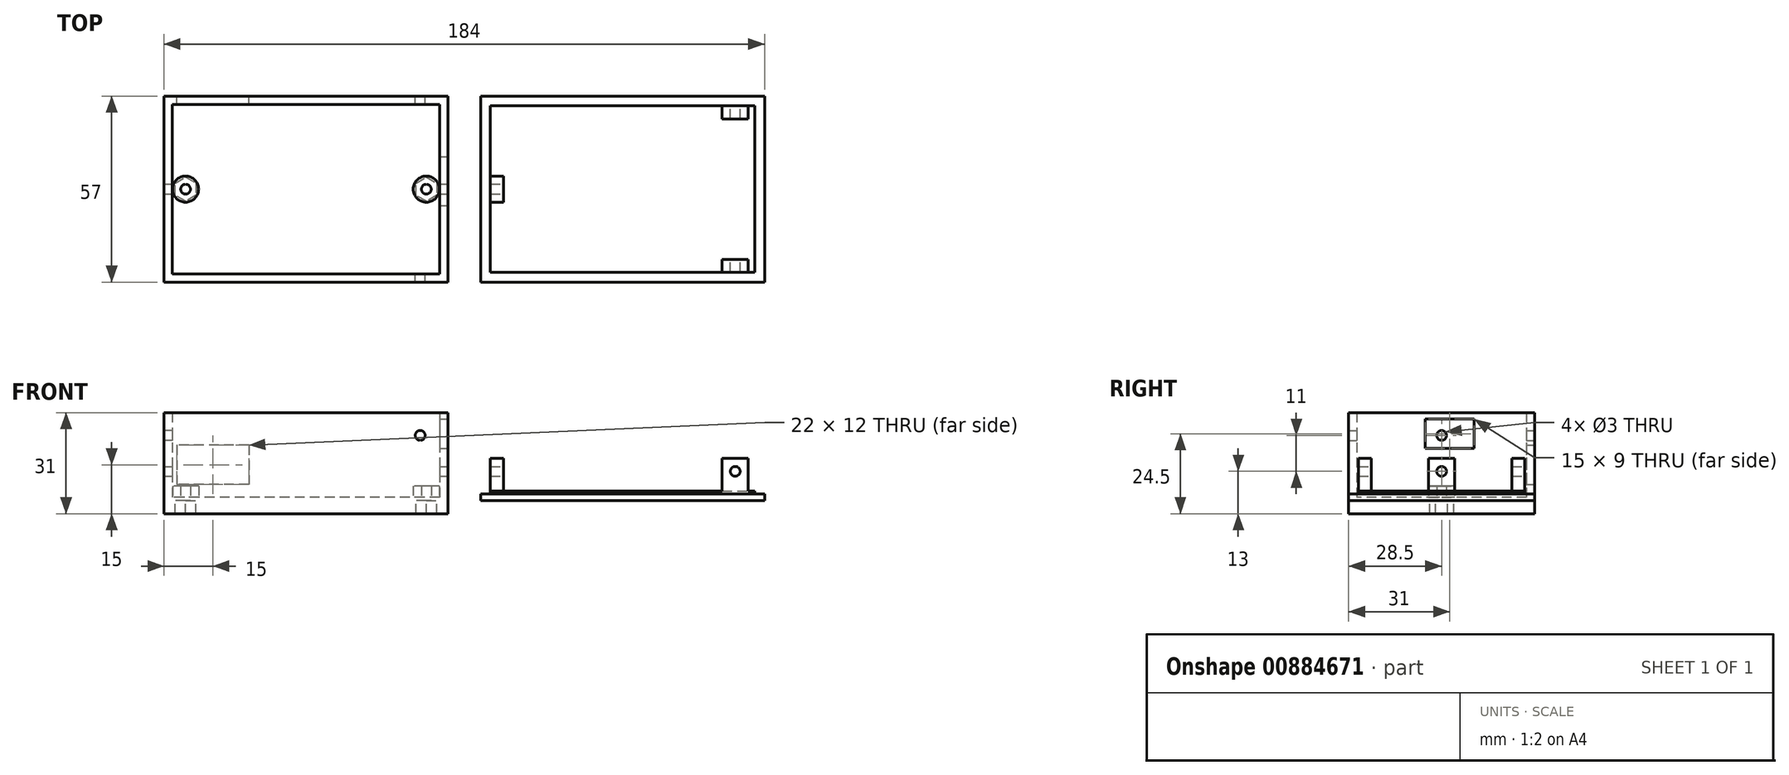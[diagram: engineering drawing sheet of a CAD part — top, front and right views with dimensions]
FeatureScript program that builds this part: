
annotation { "Feature Type Name" : "Feature", "Feature Type Description" : "" }
export const myFeature = defineFeature(function(context is Context, id is Id, definition is map)
    precondition{}
    {
        {
            assignVariable(context, id + "F0", {"name" : "wThickness", "anyValue" : 2.5});
        }
        {
            assignVariable(context, id + "F1", {"name" : "bThickness", "anyValue" : 5});
        }
        {
            assignVariable(context, id + "F2", {"name" : "nutThick", "anyValue" : 4});
        }
        {
            var Q0;
            Q0=qCreatedBy(makeId("Top.planeOp"),FACE);
            var sketch = newSketch(context, id + "F3", { "sketchPlane" : qUnion([Q0])});
            skLineSegment(sketch, "E0.bottom", {"start": v(0, 0) * mm, "end": v(87, 0) * mm});
            skLineSegment(sketch, "E0.top", {"start": v(0, 57) * mm, "end": v(87, 57) * mm});
            skLineSegment(sketch, "E0.left", {"start": v(0, 0) * mm, "end": v(0, 57) * mm});
            skLineSegment(sketch, "E0.right", {"start": v(87, 0) * mm, "end": v(87, 57) * mm});
            skLineSegment(sketch, "E1.bottom", {"start": v(2.5, 2.5) * mm, "end": v(84.5, 2.5) * mm});
            skLineSegment(sketch, "E1.top", {"start": v(2.5, 54.5) * mm, "end": v(84.5, 54.5) * mm});
            skLineSegment(sketch, "E1.left", {"start": v(2.5, 2.5) * mm, "end": v(2.5, 54.5) * mm});
            skLineSegment(sketch, "E1.right", {"start": v(84.5, 2.5) * mm, "end": v(84.5, 54.5) * mm});
            skLineSegment(sketch, "E2", {"start": v(2.5, 2.5) * mm, "end": v(2.5, 0) * mm, "construction": true});
            skLineSegment(sketch, "E3", {"start": v(2.5, 2.5) * mm, "end": v(0, 2.5) * mm, "construction": true});
            skLineSegment(sketch, "E4", {"start": v(43.5, 54.5) * mm, "end": v(43.5, 2.5) * mm, "construction": true});
            skLineSegment(sketch, "E5", {"start": v(43.5, 28.5) * mm, "end": v(6.63, 28.5) * mm, "construction": true});
            skCircle(sketch, "E6", {"center": v(6.63, 28.5) * mm, "radius": 1.5 * mm});
            skCircle(sketch, "E7.cCircle", {"center": v(6.63, 28.5) * mm, "radius": 3.2 * mm, "construction": true});
            skLineSegment(sketch, "E7.0", {"start": v(9.83, 30.35) * mm, "end": v(9.83, 26.65) * mm});
            skLineSegment(sketch, "E7.1", {"start": v(9.83, 26.65) * mm, "end": v(6.63, 24.8) * mm});
            skLineSegment(sketch, "E7.2", {"start": v(6.63, 24.8) * mm, "end": v(3.43, 26.65) * mm});
            skLineSegment(sketch, "E7.3", {"start": v(3.43, 26.65) * mm, "end": v(3.43, 30.35) * mm});
            skLineSegment(sketch, "E7.4", {"start": v(3.43, 30.35) * mm, "end": v(6.63, 32.2) * mm});
            skLineSegment(sketch, "E7.5", {"start": v(6.63, 32.2) * mm, "end": v(9.83, 30.35) * mm});
            skPoint(sketch, "E7.0.midPoint", {"position": v(9.83, 28.5) * mm});
            skCircle(sketch, "E8", {"center": v(80.38, 28.5) * mm, "radius": 1.5 * mm});
            skCircle(sketch, "E9.cCircle", {"center": v(80.38, 28.5) * mm, "radius": 3.2 * mm, "construction": true});
            skLineSegment(sketch, "E9.0", {"start": v(83.58, 30.35) * mm, "end": v(83.58, 26.65) * mm});
            skLineSegment(sketch, "E9.1", {"start": v(83.57, 26.65) * mm, "end": v(80.37, 24.8) * mm});
            skLineSegment(sketch, "E9.2", {"start": v(80.38, 24.8) * mm, "end": v(77.18, 26.65) * mm});
            skLineSegment(sketch, "E9.3", {"start": v(77.17, 26.65) * mm, "end": v(77.17, 30.35) * mm});
            skLineSegment(sketch, "E9.4", {"start": v(77.17, 30.35) * mm, "end": v(80.37, 32.2) * mm});
            skLineSegment(sketch, "E9.5", {"start": v(80.38, 32.2) * mm, "end": v(83.58, 30.35) * mm});
            skPoint(sketch, "E9.0.midPoint", {"position": v(83.58, 28.5) * mm});
            skLineSegment(sketch, "E10", {"start": v(43.5, 28.5) * mm, "end": v(80.38, 28.5) * mm, "construction": true});
            skPoint(sketch, "E11", {"position": v(77.17, 28.5) * mm});
            skLineSegment(sketch, "E12", {"start": v(87, 57) * mm, "end": v(97, 57) * mm, "construction": true});
            skLineSegment(sketch, "E13.bottom", {"start": v(97, 57) * mm, "end": v(184, 57) * mm});
            skLineSegment(sketch, "E13.top", {"start": v(97, 0) * mm, "end": v(184, 0) * mm});
            skLineSegment(sketch, "E13.left", {"start": v(97, 57) * mm, "end": v(97, 0) * mm});
            skLineSegment(sketch, "E13.right", {"start": v(184, 57) * mm, "end": v(184, 0) * mm});
            skLineSegment(sketch, "E14.bottom", {"start": v(181, 3) * mm, "end": v(100, 3) * mm});
            skLineSegment(sketch, "E14.top", {"start": v(181, 54) * mm, "end": v(100, 54) * mm});
            skLineSegment(sketch, "E14.left", {"start": v(181, 3) * mm, "end": v(181, 54) * mm});
            skLineSegment(sketch, "E14.right", {"start": v(100, 3) * mm, "end": v(100, 54) * mm});
            skLineSegment(sketch, "E15", {"start": v(100, 3) * mm, "end": v(97, 3) * mm, "construction": true});
            skLineSegment(sketch, "E16", {"start": v(100, 3) * mm, "end": v(100, 0) * mm, "construction": true});
            skSolve(sketch);
        }
        {
            var Q0;
            Q0=makeQuery(id+"F3.imprint","IMPRINT",FACE,{"disambiguationData":[TD([[makeQuery(id+"F3.imprint","IMPRINT",EDGE,{"derivedFrom":sQuery(id+"F3.wireOp",EDGE,"E0.bottom")}),1.0]])]});
            var Q1;
            Q1=makeQuery(id+"F3.imprint","IMPRINT",FACE,{"disambiguationData":[TD([[makeQuery(id+"F3.imprint","IMPRINT",EDGE,{"derivedFrom":sQuery(id+"F3.wireOp",EDGE,"E1.bottom")}),1.0]])]});
            extrude(context, id + "F4", {"entities" : qUnion([Q0, Q1]), "oppositeDirection" : true, "depth" : (getVariable(context, 'nutThick')) * mm, "offsetDistance" : 25 * mm});
        }
        {
            var Q0;
            Q0=makeQuery(id+"F3.imprint","IMPRINT",FACE,{"disambiguationData":[TD([[makeQuery(id+"F3.imprint","IMPRINT",EDGE,{"derivedFrom":sQuery(id+"F3.wireOp",EDGE,"E1.bottom")}),1.0]])]});
            var Q1;
            Q1=makeQuery(id+"F3.imprint","IMPRINT",FACE,{"disambiguationData":[TD([[makeQuery(id+"F3.imprint","IMPRINT",EDGE,{"derivedFrom":sQuery(id+"F3.wireOp",EDGE,"E0.bottom")}),1.0]])]});
            var Q2;
            Q2=makeQuery(id+"F3.imprint","IMPRINT",FACE,{"disambiguationData":[TD([[makeQuery(id+"F3.imprint","IMPRINT",EDGE,{"derivedFrom":sQuery(id+"F3.wireOp",EDGE,"E6")}),-1.0]])]});
            var Q3;
            Q3=makeQuery(id+"F3.imprint","IMPRINT",FACE,{"disambiguationData":[TD([[makeQuery(id+"F3.imprint","IMPRINT",EDGE,{"derivedFrom":sQuery(id+"F3.wireOp",EDGE,"E8")}),-1.0]])]});
            extrude(context, id + "F5", {"entities" : qUnion([Q0, Q1, Q2, Q3]), "operationType" : NewBodyOperationType.ADD, "depth" : (getVariable(context, 'bThickness') - getVariable(context, 'nutThick')) * mm, "offsetDistance" : 25 * mm});
        }
        {
            assignVariable(context, id + "F6", {"name" : "screwBlockH", "anyValue" : 3.5});
        }
        {
            var Q0;
            Q0=makeQuery(id+"F5.opExtrude","CAP_FACE",FACE,{"disambiguationData":[OSD([sQuery(id+"F3.wireOp",EDGE,"E0.bottom"),sQuery(id+"F3.wireOp",EDGE,"E0.top"),sQuery(id+"F3.wireOp",EDGE,"E0.left"),sQuery(id+"F3.wireOp",EDGE,"E0.right"),sQuery(id+"F3.wireOp",EDGE,"E6"),sQuery(id+"F3.wireOp",EDGE,"E8")])],"isStart":false});
            var sketch = newSketch(context, id + "F7", { "sketchPlane" : qUnion([Q0])});
            skPoint(sketch, "E17.0", {"position": v(6.63, 28.5) * mm});
            skCircle(sketch, "E18", {"center": v(6.63, 28.5) * mm, "radius": 4 * mm});
            skPoint(sketch, "E19.0", {"position": v(80.38, 28.5) * mm});
            skCircle(sketch, "E20", {"center": v(80.38, 28.5) * mm, "radius": 4 * mm});
            skSolve(sketch);
        }
        {
            var Q0;
            Q0=makeQuery(id+"F7.imprint","IMPRINT",FACE,{"disambiguationData":[TD([[makeQuery(id+"F7.imprint","IMPRINT",EDGE,{"derivedFrom":sQuery(id+"F7.wireOp",EDGE,"E18")}),1.0]])]});
            var Q1;
            Q1=makeQuery(id+"F7.imprint","IMPRINT",FACE,{"disambiguationData":[TD([[makeQuery(id+"F7.imprint","IMPRINT",EDGE,{"derivedFrom":sQuery(id+"F7.wireOp",EDGE,"E20")}),1.0]])]});
            extrude(context, id + "F8", {"entities" : qUnion([Q0, Q1]), "operationType" : NewBodyOperationType.ADD, "depth" : (getVariable(context, 'screwBlockH')) * mm, "offsetDistance" : 25 * mm});
        }
        {
            assignVariable(context, id + "F9", {"name" : "wallHeight", "anyValue" : 26});
        }
        {
            var Q0;
            Q0=makeQuery(id+"F3.imprint","IMPRINT",FACE,{"disambiguationData":[TD([[makeQuery(id+"F3.imprint","IMPRINT",EDGE,{"derivedFrom":sQuery(id+"F3.wireOp",EDGE,"E0.bottom")}),1.0]])]});
            extrude(context, id + "F10", {"entities" : qUnion([Q0]), "operationType" : NewBodyOperationType.ADD, "depth" : (getVariable(context, 'wallHeight') + (getVariable(context, 'bThickness') - getVariable(context, 'nutThick'))) * mm, "offsetDistance" : 25 * mm});
        }
        {
            var Q0;
            {var subQ0=sQuery(id+"F3.wireOp",EDGE,"E0.right");Q0=makeQuery(id+"F10.boolean.opBoolean","MERGE",FACE,{"derivedFrom":[makeQuery(id+"F5.boolean.opBoolean","MERGE",FACE,{"derivedFrom":[makeQuery(id+"F4.opExtrude","SWEPT_FACE",FACE,{"disambiguationData":[OSD([subQ0])]}),makeQuery(id+"F5.opExtrude","SWEPT_FACE",FACE,{"disambiguationData":[OSD([subQ0])]})]}),makeQuery(id+"F10.opExtrude","SWEPT_FACE",FACE,{"disambiguationData":[OSD([subQ0])]})]});}
            var sketch = newSketch(context, id + "F11", { "sketchPlane" : qUnion([Q0])});
            skLineSegment(sketch, "E21.bottom", {"start": v(23.5, 25) * mm, "end": v(38.5, 25) * mm});
            skLineSegment(sketch, "E21.top", {"start": v(23.5, 16) * mm, "end": v(38.5, 16) * mm});
            skLineSegment(sketch, "E21.left", {"start": v(23.5, 25) * mm, "end": v(23.5, 16) * mm});
            skLineSegment(sketch, "E21.right", {"start": v(38.5, 25) * mm, "end": v(38.5, 16) * mm});
            skLineSegment(sketch, "E22", {"start": v(38.5, 16) * mm, "end": v(38.5, -4) * mm, "construction": true});
            skLineSegment(sketch, "E23", {"start": v(31, 25) * mm, "end": v(57, 25) * mm, "construction": true});
            skSolve(sketch);
        }
        {
            var Q0;
            Q0=makeQuery(id+"F11.imprint","IMPRINT",FACE,{"disambiguationData":[TD([[makeQuery(id+"F11.imprint","IMPRINT",EDGE,{"derivedFrom":sQuery(id+"F11.wireOp",EDGE,"E21.bottom")}),-1.0]])]});
            extrude(context, id + "F12", {"entities" : qUnion([Q0]), "operationType" : NewBodyOperationType.REMOVE, "endBound" : BoundingType.UP_TO_NEXT, "oppositeDirection" : true, "depth" : 25 * mm, "offsetDistance" : 25 * mm});
        }
        {
            var Q0;
            {var subQ0=sQuery(id+"F3.wireOp",EDGE,"E0.top");Q0=makeQuery(id+"F10.boolean.opBoolean","MERGE",FACE,{"derivedFrom":[makeQuery(id+"F5.boolean.opBoolean","MERGE",FACE,{"derivedFrom":[makeQuery(id+"F4.opExtrude","SWEPT_FACE",FACE,{"disambiguationData":[OSD([subQ0])]}),makeQuery(id+"F5.opExtrude","SWEPT_FACE",FACE,{"disambiguationData":[OSD([subQ0])]})]}),makeQuery(id+"F10.opExtrude","SWEPT_FACE",FACE,{"disambiguationData":[OSD([subQ0])]})]});}
            var sketch = newSketch(context, id + "F13", { "sketchPlane" : qUnion([Q0])});
            skLineSegment(sketch, "E24.bottom", {"start": v(-26, 17) * mm, "end": v(-4, 17) * mm});
            skLineSegment(sketch, "E24.top", {"start": v(-26, 5) * mm, "end": v(-4, 5) * mm});
            skLineSegment(sketch, "E24.left", {"start": v(-26, 17) * mm, "end": v(-26, 5) * mm});
            skLineSegment(sketch, "E24.right", {"start": v(-4, 17) * mm, "end": v(-4, 5) * mm});
            skLineSegment(sketch, "E25", {"start": v(-26, 5) * mm, "end": v(-26, -4) * mm, "construction": true});
            skLineSegment(sketch, "E26", {"start": v(-4, 5) * mm, "end": v(0, 5) * mm, "construction": true});
            skPoint(sketch, "E27.0", {"position": v(-84.5, 27) * mm});
            skLineSegment(sketch, "E28", {"start": v(-84.5, 27) * mm, "end": v(-72.5, 27) * mm, "construction": true});
            skLineSegment(sketch, "E29", {"start": v(-78.5, 27) * mm, "end": v(-78.5, 20) * mm, "construction": true});
            skCircle(sketch, "E30", {"center": v(-78.5, 20) * mm, "radius": 1.5 * mm});
            skSolve(sketch);
        }
        {
            var Q0;
            Q0=makeQuery(id+"F13.imprint","IMPRINT",FACE,{"disambiguationData":[TD([[makeQuery(id+"F13.imprint","IMPRINT",EDGE,{"derivedFrom":sQuery(id+"F13.wireOp",EDGE,"E24.bottom")}),-1.0]])]});
            extrude(context, id + "F14", {"entities" : qUnion([Q0]), "operationType" : NewBodyOperationType.REMOVE, "oppositeDirection" : true, "depth" : (getVariable(context, 'wThickness')) * mm, "offsetDistance" : 25 * mm});
        }
        {
            var Q0;
            Q0=makeQuery(id+"F13.imprint","IMPRINT",FACE,{"disambiguationData":[TD([[makeQuery(id+"F13.imprint","IMPRINT",EDGE,{"derivedFrom":sQuery(id+"F13.wireOp",EDGE,"E30")}),1.0]])]});
            extrude(context, id + "F15", {"entities" : qUnion([Q0]), "operationType" : NewBodyOperationType.REMOVE, "endBound" : BoundingType.THROUGH_ALL, "oppositeDirection" : true, "depth" : 25 * mm, "offsetDistance" : 25 * mm});
        }
        {
            assignVariable(context, id + "F16", {"name" : "lidThick1", "anyValue" : 3});
        }
        {
            assignVariable(context, id + "F17", {"name" : "lidThick2", "anyValue" : 2});
        }
        {
            var Q0;
            Q0=makeQuery(id+"F3.imprint","IMPRINT",FACE,{"disambiguationData":[TD([[makeQuery(id+"F3.imprint","IMPRINT",EDGE,{"derivedFrom":sQuery(id+"F3.wireOp",EDGE,"E14.bottom")}),-1.0]])]});
            extrude(context, id + "F18", {"entities" : qUnion([Q0]), "depth" : (getVariable(context, 'lidThick1')) * mm, "offsetDistance" : 25 * mm});
        }
        {
            var Q0;
            Q0=makeQuery(id+"F3.imprint","IMPRINT",FACE,{"disambiguationData":[TD([[makeQuery(id+"F3.imprint","IMPRINT",EDGE,{"derivedFrom":sQuery(id+"F3.wireOp",EDGE,"E13.bottom")}),-1.0]])]});
            extrude(context, id + "F19", {"entities" : qUnion([Q0]), "operationType" : NewBodyOperationType.ADD, "depth" : (getVariable(context, 'lidThick2')) * mm, "offsetDistance" : 25 * mm});
        }
        {
            var Q0;
            Q0=makeQuery(id+"F18.opExtrude","CAP_FACE",FACE,{"disambiguationData":[OSD([sQuery(id+"F3.wireOp",EDGE,"E14.bottom"),sQuery(id+"F3.wireOp",EDGE,"E14.top"),sQuery(id+"F3.wireOp",EDGE,"E14.left"),sQuery(id+"F3.wireOp",EDGE,"E14.right")])],"isStart":false});
            var sketch = newSketch(context, id + "F20", { "sketchPlane" : qUnion([Q0])});
            skLineSegment(sketch, "E31", {"start": v(179, 50) * mm, "end": v(179, 54) * mm});
            skLineSegment(sketch, "E32", {"start": v(171, 50) * mm, "end": v(171, 54) * mm});
            skLineSegment(sketch, "E33", {"start": v(171, 50) * mm, "end": v(179, 50) * mm});
            skLineSegment(sketch, "E34", {"start": v(179, 3) * mm, "end": v(179, 7) * mm});
            skLineSegment(sketch, "E35", {"start": v(171, 3) * mm, "end": v(171, 7) * mm});
            skLineSegment(sketch, "E36", {"start": v(171, 7) * mm, "end": v(179, 7) * mm});
            skLineSegment(sketch, "E37", {"start": v(104, 32.5) * mm, "end": v(100, 32.5) * mm});
            skLineSegment(sketch, "E38", {"start": v(104, 24.5) * mm, "end": v(100, 24.5) * mm});
            skLineSegment(sketch, "E39", {"start": v(104, 32.5) * mm, "end": v(104, 24.5) * mm});
            skSolve(sketch);
        }
        {
            var Q0;
            {var subQ0=sQuery(id+"F20.wireOp",EDGE,"E31");Q0=makeQuery(id+"F20.imprint","IMPRINT",FACE,{"disambiguationData":[TD([[makeQuery(id+"F20.imprint","IMPRINT",EDGE,{"derivedFrom":subQ0}),1.0]])]});}
            var Q1;
            {var subQ0=sQuery(id+"F20.wireOp",EDGE,"E34");Q1=makeQuery(id+"F20.imprint","IMPRINT",FACE,{"disambiguationData":[TD([[makeQuery(id+"F20.imprint","IMPRINT",EDGE,{"derivedFrom":subQ0}),1.0]])]});}
            var Q2;
            {var subQ0=sQuery(id+"F20.wireOp",EDGE,"E37");Q2=makeQuery(id+"F20.imprint","IMPRINT",FACE,{"disambiguationData":[TD([[makeQuery(id+"F20.imprint","IMPRINT",EDGE,{"derivedFrom":subQ0}),1.0]])]});}
            extrude(context, id + "F21", {"entities" : qUnion([Q0, Q1, Q2]), "operationType" : NewBodyOperationType.ADD, "depth" : 10 * mm, "offsetDistance" : 25 * mm});
        }
        {
            var Q0;
            {var subQ0=sQuery(id+"F3.wireOp",EDGE,"E14.top");Q0=makeQuery(id+"F21.boolean.opBoolean","MERGE",FACE,{"derivedFrom":[makeQuery(id+"F18.opExtrude","SWEPT_FACE",FACE,{"disambiguationData":[OSD([subQ0])]}),makeQuery(id+"F21.opExtrude","SWEPT_FACE",FACE,{"disambiguationData":[OSD([subQ0])]})]});}
            var sketch = newSketch(context, id + "F22", { "sketchPlane" : qUnion([Q0])});
            skCircle(sketch, "E40", {"center": v(-175, 9) * mm, "radius": 1.5 * mm});
            skLineSegment(sketch, "E41", {"start": v(-175, 9) * mm, "end": v(-175, 13) * mm, "construction": true});
            skSolve(sketch);
        }
        {
            var Q0;
            Q0=makeQuery(id+"F21.opExtrude","SWEPT_FACE",FACE,{"disambiguationData":[OSD([sQuery(id+"F20.wireOp",EDGE,"E39")])]});
            var sketch = newSketch(context, id + "F23", { "sketchPlane" : qUnion([Q0])});
            skLineSegment(sketch, "E42", {"start": v(28.5, 13) * mm, "end": v(28.5, 9) * mm, "construction": true});
            skCircle(sketch, "E43", {"center": v(28.5, 9) * mm, "radius": 1.5 * mm});
            skSolve(sketch);
        }
        {
            var Q0;
            Q0=makeQuery(id+"F22.imprint","IMPRINT",FACE,{"disambiguationData":[TD([[makeQuery(id+"F22.imprint","IMPRINT",EDGE,{"derivedFrom":sQuery(id+"F22.wireOp",EDGE,"E40")}),1.0]])]});
            extrude(context, id + "F24", {"entities" : qUnion([Q0]), "operationType" : NewBodyOperationType.REMOVE, "endBound" : BoundingType.THROUGH_ALL, "oppositeDirection" : true, "depth" : 25 * mm, "offsetDistance" : 25 * mm});
        }
        {
            var Q0;
            Q0=makeQuery(id+"F23.imprint","IMPRINT",FACE,{"disambiguationData":[TD([[makeQuery(id+"F23.imprint","IMPRINT",EDGE,{"derivedFrom":sQuery(id+"F23.wireOp",EDGE,"E43")}),1.0]])]});
            extrude(context, id + "F25", {"entities" : qUnion([Q0]), "operationType" : NewBodyOperationType.REMOVE, "endBound" : BoundingType.THROUGH_ALL, "oppositeDirection" : true, "depth" : 25 * mm, "offsetDistance" : 25 * mm});
        }
        {
            var Q0;
            {var subQ0=sQuery(id+"F3.wireOp",EDGE,"E0.left");Q0=makeQuery(id+"F10.boolean.opBoolean","MERGE",FACE,{"derivedFrom":[makeQuery(id+"F5.boolean.opBoolean","MERGE",FACE,{"derivedFrom":[makeQuery(id+"F4.opExtrude","SWEPT_FACE",FACE,{"disambiguationData":[OSD([subQ0])]}),makeQuery(id+"F5.opExtrude","SWEPT_FACE",FACE,{"disambiguationData":[OSD([subQ0])]})]}),makeQuery(id+"F10.opExtrude","SWEPT_FACE",FACE,{"disambiguationData":[OSD([subQ0])]})]});}
            var sketch = newSketch(context, id + "F26", { "sketchPlane" : qUnion([Q0])});
            skLineSegment(sketch, "E44", {"start": v(-28.5, 27) * mm, "end": v(-28.5, 20) * mm, "construction": true});
            skCircle(sketch, "E45", {"center": v(-28.5, 20) * mm, "radius": 1.5 * mm});
            skSolve(sketch);
        }
        {
            var Q0;
            Q0=makeQuery(id+"F26.imprint","IMPRINT",FACE,{"disambiguationData":[TD([[makeQuery(id+"F26.imprint","IMPRINT",EDGE,{"derivedFrom":sQuery(id+"F26.wireOp",EDGE,"E45")}),1.0]])]});
            extrude(context, id + "F27", {"entities" : qUnion([Q0]), "operationType" : NewBodyOperationType.REMOVE, "endBound" : BoundingType.UP_TO_NEXT, "oppositeDirection" : true, "depth" : 25 * mm, "offsetDistance" : 25 * mm});
        }
    });
